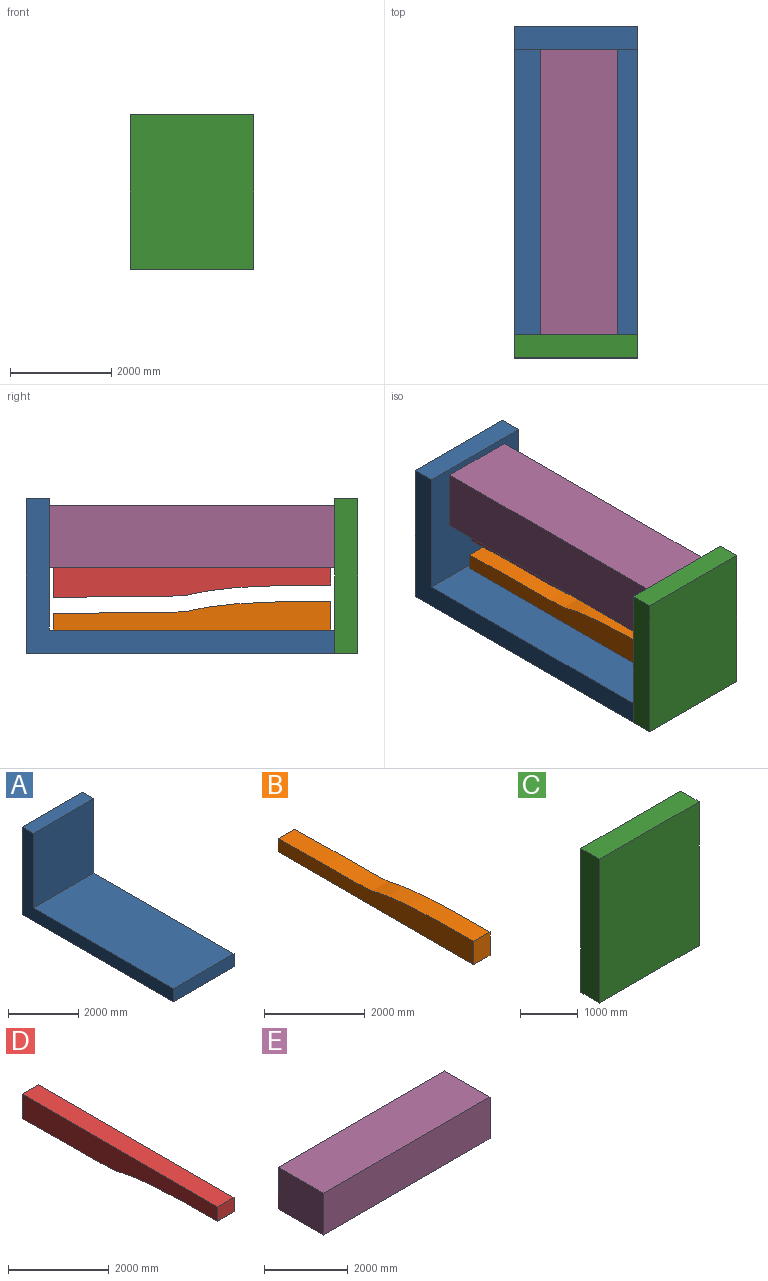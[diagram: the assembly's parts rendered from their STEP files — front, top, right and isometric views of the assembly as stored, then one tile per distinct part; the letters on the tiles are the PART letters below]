
ASSEMBLY  parts=5 mates=4
PART A: 8 faces, bbox 2438.4x6096x3048 mm
  f0: plane 2590.8x2438.4mm, normal (0,-1,0), area 6317406.7mm2, adj f1,f2,f4,f7
  f1: plane 6096x3048mm, normal (-1,0,0), area 3971605mm2, adj f0,f3,f4,f5,f6,f7
  f2: plane 6096x3048mm, normal (1,0,0), area 3971605mm2, adj f0,f3,f4,f5,f6,f7
  f3: plane 3048x2438.4mm, normal (0,1,0), area 7432243.2mm2, adj f1,f2,f4,f5
  f4: plane 2438.4x457.2mm, normal (0,0,1), area 1114836.5mm2, adj f0,f1,f2,f3
  f5: plane 6096x2438.4mm, normal (0,0,-1), area 14864486.4mm2, adj f1,f2,f3,f6
  f6: plane 2438.4x457.2mm, normal (0,-1,0), area 1114836.5mm2, adj f1,f2,f5,f7
  f7: plane 5638.8x2438.4mm, normal (0,0,1), area 13749649.9mm2, adj f0,f1,f2,f6
PART B: 6 faces, bbox 457.2x5486.4x577 mm
  f0: plane 567.59x457.2mm, normal (0,-1,0), area 259500.7mm2, adj f1,f3,f4,f5
  f1: plane 5486.4x457.2mm, normal (0,0,-1), area 2508382.1mm2, adj f0,f2,f4,f5
  f2: plane 457.2x317.5mm, normal (0,1,0), area 145159.7mm2, adj f1,f3,f4,f5
  f3: extruded ~5486.4x457.2mm, area 2517536.5mm2, adj f0,f2,f4,f5
  f4: plane 5486.4x577.01mm, normal (1,0,0), area 2375297.3mm2, adj f0,f1,f2,f3
  f5: plane 5486.4x577.01mm, normal (-1,0,0), area 2375297.3mm2, adj f0,f1,f2,f3
PART C: 6 faces, bbox 2438.4x457.2x3048 mm
  f0: plane 3048x457.2mm, normal (-1,0,0), area 1393545.6mm2, adj f1,f3,f4,f5
  f1: plane 3048x2438.4mm, normal (0,-1,0), area 7432243.2mm2, adj f0,f2,f4,f5
  f2: plane 3048x457.2mm, normal (1,0,0), area 1393545.6mm2, adj f1,f3,f4,f5
  f3: plane 3048x2438.4mm, normal (0,1,0), area 7432243.2mm2, adj f0,f2,f4,f5
  f4: plane 2438.4x457.2mm, normal (0,0,1), area 1114836.5mm2, adj f0,f1,f2,f3
  f5: plane 2438.4x457.2mm, normal (0,0,-1), area 1114836.5mm2, adj f0,f1,f2,f3
PART D: 6 faces, bbox 457.2x5486.4x598.1 mm
  f0: plane 457.2x346.81mm, normal (0,-1,0), area 158562.9mm2, adj f1,f3,f4,f5
  f1: extruded ~5486.4x457.2mm, area 2517536.5mm2, adj f0,f2,f4,f5
  f2: plane 596.9x457.2mm, normal (0,1,0), area 272904mm2, adj f1,f3,f4,f5
  f3: plane 5486.4x457.2mm, normal (0,0,1), area 2508382.1mm2, adj f0,f2,f4,f5
  f4: plane 5486.4x598.09mm, normal (1,0,0), area 2641466.8mm2, adj f0,f1,f2,f3
  f5: plane 5486.4x598.09mm, normal (-1,0,0), area 2641466.8mm2, adj f0,f1,f2,f3
PART E: 6 faces, bbox 5638.8x1524x1219.2 mm
  f0: plane 1524x1219.2mm, normal (-1,0,0), area 1858060.8mm2, adj f1,f3,f4,f5
  f1: plane 5638.8x1219.2mm, normal (0,-1,0), area 6874825mm2, adj f0,f2,f4,f5
  f2: plane 1524x1219.2mm, normal (1,0,0), area 1858060.8mm2, adj f1,f3,f4,f5
  f3: plane 5638.8x1219.2mm, normal (0,1,0), area 6874825mm2, adj f0,f2,f4,f5
  f4: plane 5638.8x1524mm, normal (0,0,1), area 8593531.2mm2, adj f0,f1,f2,f3
  f5: plane 5638.8x1524mm, normal (0,0,-1), area 8593531.2mm2, adj f0,f1,f2,f3
PLACE A t=(-2438.4,0,0)mm
PLACE B t=(-1447.8,533.4,457.2)mm
PLACE C t=(-2438.4,0,0)mm
PLACE D t=(-1393.72,533.4,777.8)mm
PLACE E rot(axis=(0,0,1),90deg) t=(-403.12,457.2,1692.2)mm
MATE fastened A.f7 <-> B.f1  axis (0,0,1) through (-1219.2,3276.6,457.2)mm
MATE fastened D.f3 <-> E.f5  axis (0,0,1) through (-1165.12,3276.6,1692.2)mm
MATE planar C.f3 <-> E.f0  axis (0,1,0) through (-1219.2,457.2,1524)mm
MATE fastened A.f5 <-> C.f5  axis (0,0,1) through (0,457.2,0)mm
